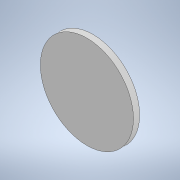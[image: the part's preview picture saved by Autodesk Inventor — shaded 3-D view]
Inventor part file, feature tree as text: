
AUTODESK INVENTOR PART (.ipt)
format: ipt  version: 2021 (Build 250183000, 183)  size: 91,136 bytes
history: native  units: mm
features: extrude x1, sketch x1
ambient origin geometry x8: Origin, YZ Plane, XZ Plane, XY Plane, X Axis, Y Axis, Z Axis, Center Point
bodies: Solid1 (feature_tree)
feature tree (2):
  extrude  "Extrusion1"  Depth=1.0mm TaperAngle=0.0deg
  sketch  "Sketch1"  dims[d0=15.0mm d1=1.0mm d2=0.0mm d3=0.5mm d4=0.872665mm]
